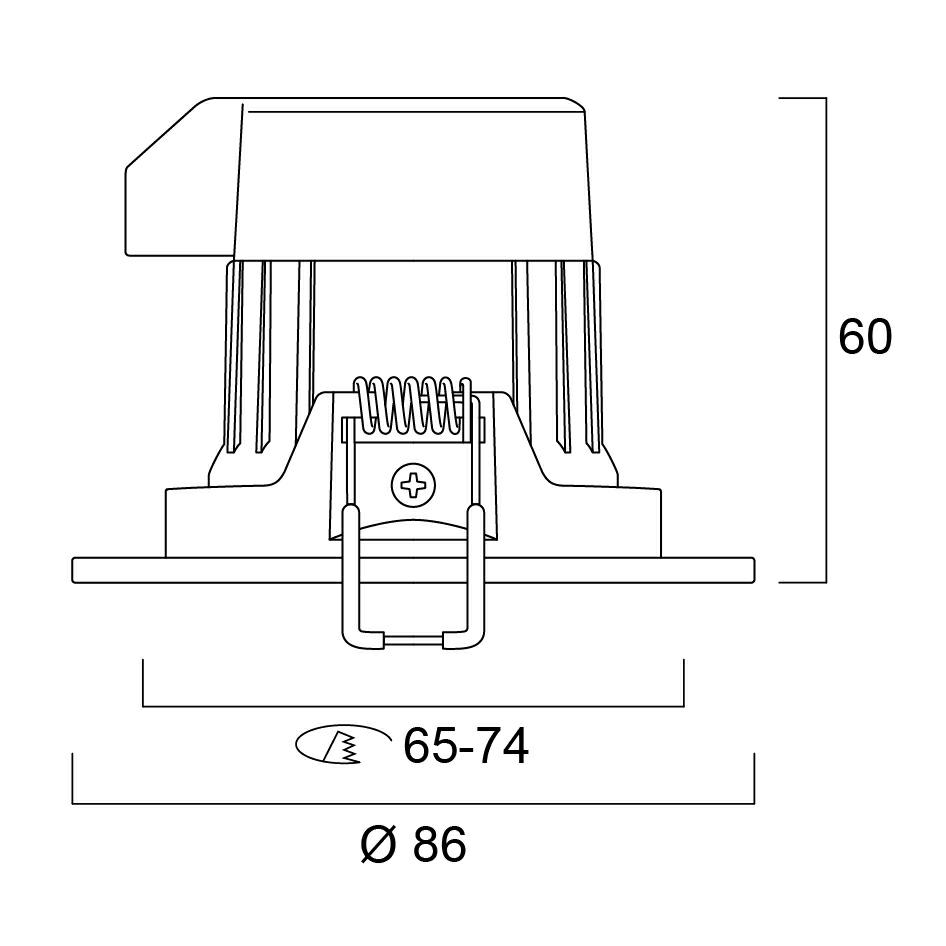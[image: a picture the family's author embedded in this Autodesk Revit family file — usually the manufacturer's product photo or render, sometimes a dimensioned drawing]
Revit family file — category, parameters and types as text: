
# Revit family: 5186
name_source: partatom
category: Lighting Fixtures
revit_build: Autodesk Revit 2018 (Build: 20170223_1515(x64)
units: mm (PartAtom-declared; Revit-internal decimal feet)

## family parameters
Cut with Voids When Loaded = No
Host = Face
Light Source = No
OmniClass Number = 23.80.70.00
OmniClass Title = Lighting
Part Type = Normal
Room Calculation Point = No
Round Connector Dimension = Use Diameter
Shared = No

## types (1)
- 0005186 START SPOT ALU 760LM 3CCT DIM IP44 BLK
    Apparent Load = 9 VA
    Assembly Code = D5020200
    AssetType = Fixed
    ClassificationName = Uniclass2015
    ClassificationValue = EF_70_80
    Cost = 0 $
    Default Elevation = 1219 mm
    DepthDiffuser_FEILO = 5 mm  [stored 0.0164042 ft]
    Description = Integrated LED recessed spotlight, vertical tilt 30°, black aluminium bezel finish, dimmable trailing/leading edge, 3-CCT changeable 2700-3000-4000K, 50° degree beam angle, polycarbonate and aluminium body, low profile 62mm recessed depth, IP44 from the front, IK03, loop-in/loop-out terminals for fast wiring, 68-72mm cutout, clear lens. Additional white or gold reflectors  can be ordered as accessory.
    DiameterBezel_FEILO = 86 mm  [stored 0.282152 ft]
    DocumentationLiterature = http://www.sylvania-lighting.com
    DurationUnit = hours
    ElectricShockClassification = 100
    ExpectedLife = 50000
    HeightBezel_FEILO = 2 mm  [stored 0.00656168 ft]
    IfcExportAs = Class II
    IfcExportType = IfcLightFixtureType
    ImpactProtectionIndex = IfcLightFixtureType
    IngressProtection = IfcLightFixtureType
    InputNominalFrequency = 3000
    InputVoltage = 0
    LampColourRenderingIndex = 16500
    LampColourTemperature = LED
    LampMacAdamStep = 80
    LampNominalLuminous = 3000 K
    LightOutputRatio = LED
    LuminaireType = 0
    ManufacturerName = 100 lm/W
    Material = Feilo Sylvania
    Material_1_FEILO = Body-Sylvania-StartSpot-White
    Material_2_FEILO = LED-Sylvania-StartSpot
    Material_3_FEILO = <By Category>
    Material_4_FEILO = <By Category>
    Model = START SPOT ALU 760LM 3CCT DIM IP44 BLK
    ModelNumber = 0005186
    ModelReference = START SPOT ALU 760LM 3CCT DIM IP44 BLK
    Name = START SPOT ALU 760LM 3CCT DIM IP44 BLK
    NominalDepth = 86 mm  [stored 0.282152 ft]
    NominalHeight = 60 mm  [stored 0.19685 ft]
    NominalLength = 86 mm  [stored 0.282152 ft]
    PowerConsumption = Lighting
    PowerFactor = 0
    RadiusCutout_FEILO = 36 mm
    RadiusDiffuser_FEILO = 14 mm  [stored 0.0459318 ft]
    RadiusOptics_FEILO = 99 mm
    Type Image = <None>
    TypeHead_FEILO = Start Spot IP20 Head : 0005184 START SPOT ALU 870LM 3CCT DIM IP44 WHT
    TypeName = START SPOT ALU 760LM 3CCT DIM IP44 BLK
    URL = 0.9
    VisibilityTop_FEILO = Yes
    Voltage = 230 V
    WarrantyDescription = http://www.sylvania-lighting.com

note: [stored X ft] marks values corroborated as IEEE doubles in the binary element streams (Revit-internal decimal feet)

## geometry (parser evidence)
native form markers: Sweep x6
no freeform markers — native parametric forms only
